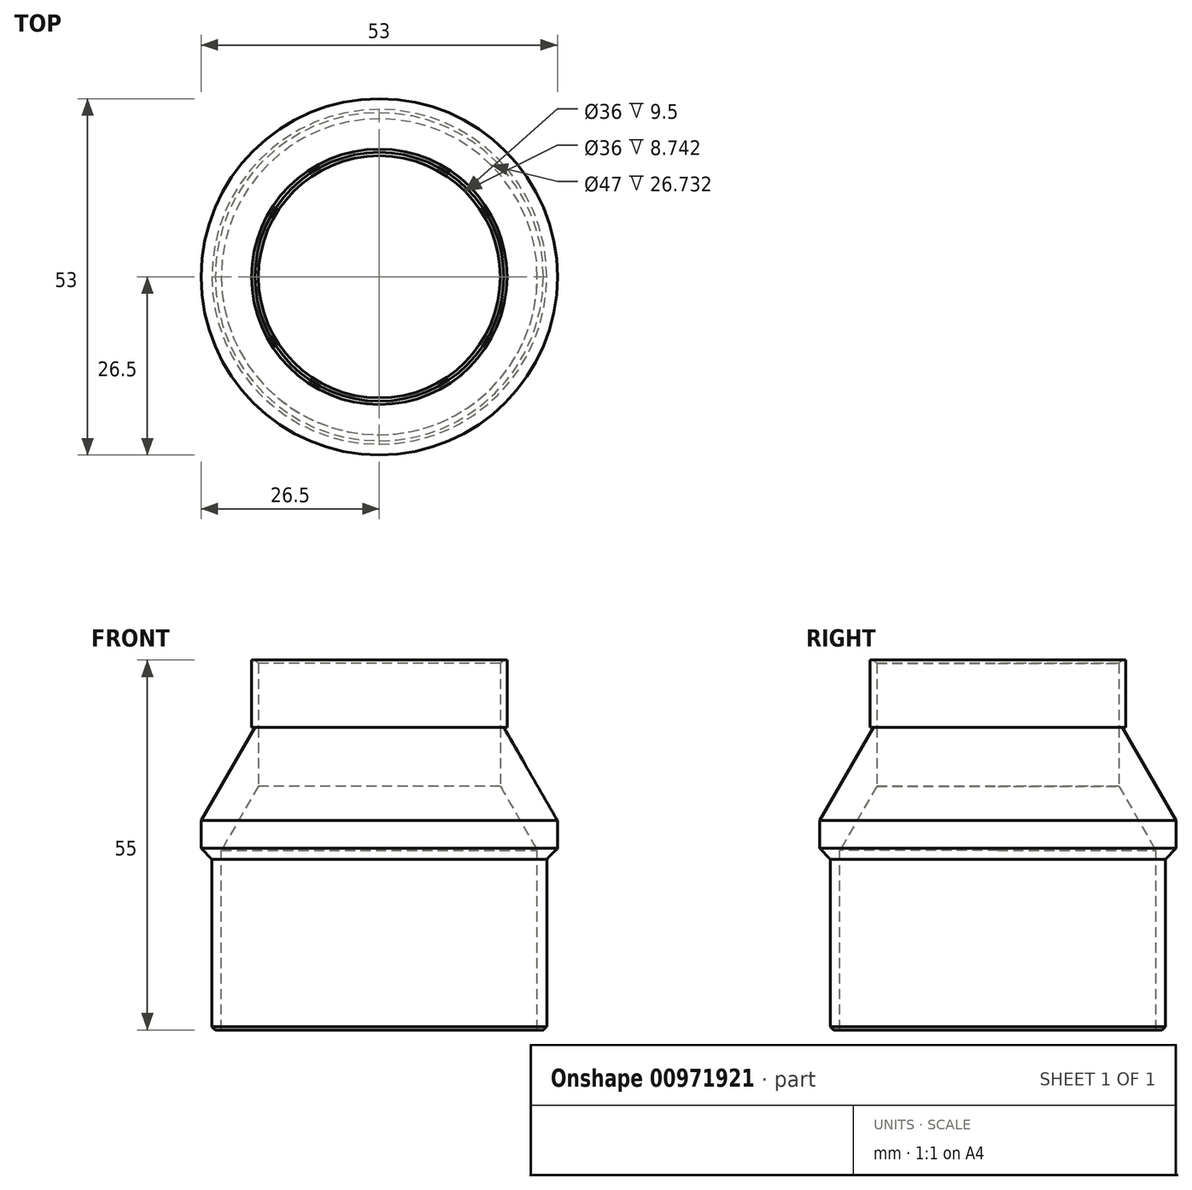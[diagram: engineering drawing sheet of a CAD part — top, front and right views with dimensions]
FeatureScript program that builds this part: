
annotation { "Feature Type Name" : "Feature", "Feature Type Description" : "" }
export const myFeature = defineFeature(function(context is Context, id is Id, definition is map)
    precondition{}
    {
        {
            var Q0;
            Q0=qCreatedBy(makeId("Top.planeOp"),FACE);
            var sketch = newSketch(context, id + "F0", { "sketchPlane" : qUnion([Q0])});
            skCircle(sketch, "E0", {"center": v(0, 0) * mm, "radius": 26.5 * mm});
            skCircle(sketch, "E1", {"center": v(0, 0) * mm, "radius": 24.9 * mm});
            skCircle(sketch, "E2", {"center": v(0, 0) * mm, "radius": 18 * mm});
            skCircle(sketch, "E3", {"center": v(0, 0) * mm, "radius": 23.5 * mm});
            skCircle(sketch, "E4", {"center": v(0, 0) * mm, "radius": 19 * mm});
            skSolve(sketch);
        }
        {
            var Q0;
            Q0=makeQuery(id+"F0.imprint","IMPRINT",FACE,{"disambiguationData":[TD([[makeQuery(id+"F0.imprint","IMPRINT",EDGE,{"derivedFrom":sQuery(id+"F0.wireOp",EDGE,"E0")}),1.0]])]});
            var Q1;
            Q1=makeQuery(id+"F0.imprint","IMPRINT",FACE,{"disambiguationData":[TD([[makeQuery(id+"F0.imprint","IMPRINT",EDGE,{"derivedFrom":sQuery(id+"F0.wireOp",EDGE,"E1")}),1.0]])]});
            var Q2;
            Q2=makeQuery(id+"F0.imprint","IMPRINT",FACE,{"disambiguationData":[TD([[makeQuery(id+"F0.imprint","IMPRINT",EDGE,{"derivedFrom":sQuery(id+"F0.wireOp",EDGE,"E3")}),1.0]])]});
            var Q3;
            Q3=makeQuery(id+"F0.imprint","IMPRINT",FACE,{"disambiguationData":[TD([[makeQuery(id+"F0.imprint","IMPRINT",EDGE,{"derivedFrom":sQuery(id+"F0.wireOp",EDGE,"E2")}),-1.0]])]});
            extrude(context, id + "F1", {"entities" : qUnion([Q0, Q1, Q2, Q3]), "depth" : 20 * mm, "offsetDistance" : 25 * mm});
        }
        {
            var Q0;
            Q0=makeQuery(id+"F0.imprint","IMPRINT",FACE,{"disambiguationData":[TD([[makeQuery(id+"F0.imprint","IMPRINT",EDGE,{"derivedFrom":sQuery(id+"F0.wireOp",EDGE,"E1")}),1.0]])]});
            extrude(context, id + "F2", {"entities" : qUnion([Q0]), "operationType" : NewBodyOperationType.ADD, "oppositeDirection" : true, "depth" : 25 * mm, "offsetDistance" : 25 * mm});
        }
        {
            var Q0;
            Q0=makeQuery(id+"F0.imprint","IMPRINT",FACE,{"disambiguationData":[TD([[makeQuery(id+"F0.imprint","IMPRINT",EDGE,{"derivedFrom":sQuery(id+"F0.wireOp",EDGE,"E2")}),-1.0]])]});
            extrude(context, id + "F3", {"entities" : qUnion([Q0]), "depth" : 30 * mm, "offsetDistance" : 25 * mm, "hasSecondDirection" : true, "secondDirectionOppositeDirection" : false, "secondDirectionDepth" : 20 * mm});
        }
        {
            var Q0;
            Q0=makeQuery(id+"F1.opExtrude","CAP_EDGE",EDGE,{"disambiguationData":[OSD([sQuery(id+"F0.wireOp",EDGE,"E0")])],"isStart":false});
            chamfer(context, id + "F4", {"entities" : qUnion([Q0]), "chamferType" : ChamferType.OFFSET_ANGLE, "width" : 8 * mm, "oppositeDirection" : false, "angle" : 60 * degree});
        }
        {
            var Q0;
            Q0=makeQuery(id+"F3.opExtrude","CAP_EDGE",EDGE,{"disambiguationData":[OSD([sQuery(id+"F0.wireOp",EDGE,"E2")])],"isStart":false});
            chamfer(context, id + "F5", {"entities" : qUnion([Q0]), "width" : 0.5 * mm, "tangentPropagation" : true});
        }
        {
            var Q0;
            Q0=makeQuery(id+"F2.opExtrude","CAP_EDGE",EDGE,{"disambiguationData":[OSD([sQuery(id+"F0.wireOp",EDGE,"E1")])],"isStart":false});
            chamfer(context, id + "F6", {"entities" : qUnion([Q0]), "width" : 0.5 * mm, "tangentPropagation" : true});
        }
        {
            var Q0;
            Q0=makeQuery(id+"F1.opExtrude","CAP_EDGE",EDGE,{"disambiguationData":[OSD([sQuery(id+"F0.wireOp",EDGE,"E0")])],"isStart":true});
            chamfer(context, id + "F7", {"entities" : qUnion([Q0]), "width" : 2 * mm, "tangentPropagation" : true});
        }
        {
            var Q0;
            Q0=makeQuery(id+"F1.opExtrude","CAP_EDGE",EDGE,{"disambiguationData":[OSD([sQuery(id+"F0.wireOp",EDGE,"E2")])],"isStart":true});
            chamfer(context, id + "F8", {"entities" : qUnion([Q0]), "chamferType" : ChamferType.OFFSET_ANGLE, "width" : 6.5 * mm, "oppositeDirection" : false, "angle" : 60 * degree, "tangentPropagation" : true});
        }
    });
